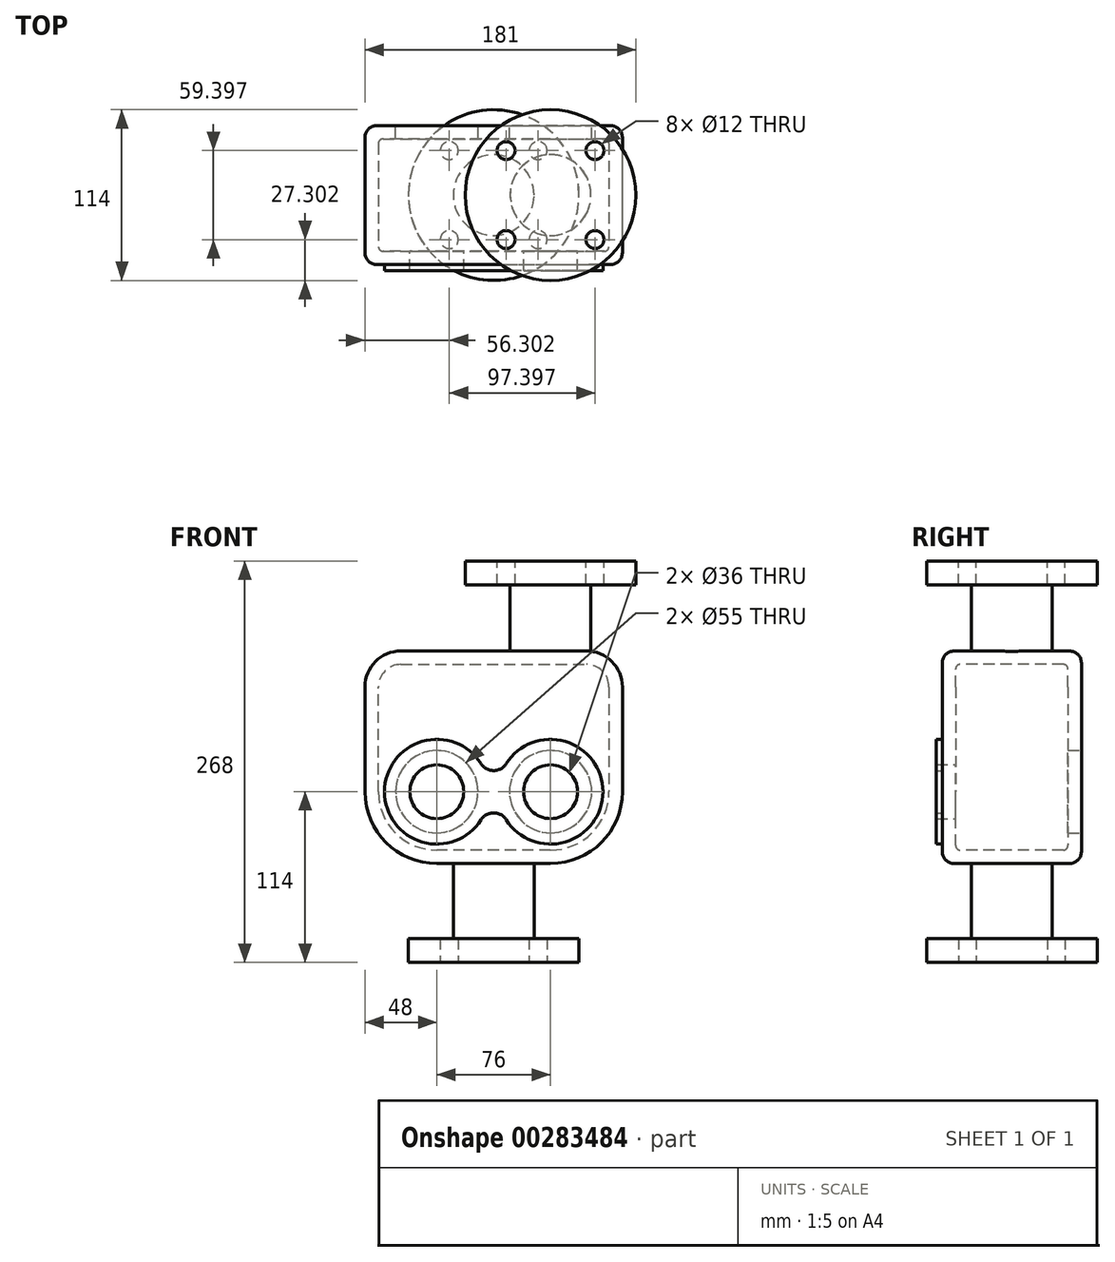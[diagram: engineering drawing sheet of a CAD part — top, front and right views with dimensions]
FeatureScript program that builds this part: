
annotation { "Feature Type Name" : "Feature", "Feature Type Description" : "" }
export const myFeature = defineFeature(function(context is Context, id is Id, definition is map)
    precondition{}
    {
        {
            var Q0;
            Q0=qCreatedBy(makeId("Top.planeOp"),FACE);
            var sketch = newSketch(context, id + "F0", { "sketchPlane" : qUnion([Q0])});
            skCircle(sketch, "E0", {"center": v(0, 0) * mm, "radius": 57 * mm});
            skCircle(sketch, "E1", {"center": v(0, 0) * mm, "radius": 42 * mm, "construction": true});
            skCircle(sketch, "E2", {"center": v(29.7, -29.7) * mm, "radius": 6 * mm});
            skLineSegment(sketch, "E3", {"start": v(0, 0) * mm, "end": v(29.7, -29.7) * mm, "construction": true});
            skCircle(sketch, "E4.MirrorC", {"center": v(-29.7, -29.7) * mm, "radius": 6 * mm});
            skCircle(sketch, "E5.MirrorC", {"center": v(-29.7, 29.7) * mm, "radius": 6 * mm});
            skCircle(sketch, "E6.MirrorC", {"center": v(29.7, 29.7) * mm, "radius": 6 * mm});
            skSolve(sketch);
        }
        {
            var Q0;
            Q0=makeQuery(id+"F0.imprint","IMPRINT",FACE,{"disambiguationData":[TD([[makeQuery(id+"F0.imprint","IMPRINT",EDGE,{"derivedFrom":sQuery(id+"F0.wireOp",EDGE,"E0")}),1.0]])]});
            extrude(context, id + "F1", {"entities" : qUnion([Q0]), "depth" : 16 * mm});
        }
        {
            var Q0;
            Q0=makeQuery(id+"F1.opExtrude","CAP_FACE",FACE,{"disambiguationData":[OSD([sQuery(id+"F0.wireOp",EDGE,"E0"),sQuery(id+"F0.wireOp",EDGE,"E2"),sQuery(id+"F0.wireOp",EDGE,"E4.MirrorC"),sQuery(id+"F0.wireOp",EDGE,"E5.MirrorC"),sQuery(id+"F0.wireOp",EDGE,"E6.MirrorC")])],"isStart":false});
            var sketch = newSketch(context, id + "F2", { "sketchPlane" : qUnion([Q0])});
            skCircle(sketch, "E7", {"center": v(0, 0) * mm, "radius": 27 * mm});
            skSolve(sketch);
        }
        {
            var Q0;
            Q0=makeQuery(id+"F2.imprint","IMPRINT",FACE,{"disambiguationData":[TD([[makeQuery(id+"F2.imprint","IMPRINT",EDGE,{"derivedFrom":sQuery(id+"F2.wireOp",EDGE,"E7")}),1.0]])]});
            extrude(context, id + "F3", {"entities" : qUnion([Q0]), "operationType" : NewBodyOperationType.ADD, "depth" : 50 * mm});
        }
        {
            var Q0;
            Q0=qCreatedBy(makeId("Front.planeOp"),FACE);
            var sketch = newSketch(context, id + "F4", { "sketchPlane" : qUnion([Q0])});
            skLineSegment(sketch, "E8.bottom", {"start": v(-62, 208) * mm, "end": v(62, 208) * mm});
            skLineSegment(sketch, "E8.top", {"start": v(-86, 114) * mm, "end": v(86, 114) * mm, "construction": true});
            skLineSegment(sketch, "E8.left", {"start": v(-86, 184) * mm, "end": v(-86, 114) * mm});
            skLineSegment(sketch, "E8.right", {"start": v(86, 184) * mm, "end": v(86, 114) * mm});
            skLineSegment(sketch, "E9", {"start": v(0, 0) * mm, "end": v(0, 370.93) * mm, "construction": true});
            skArc(sketch, "E10", {"start": v(-86, 114) * mm, "mid": v(-71.94, 80.06) * mm, "end": v(-38, 66) * mm});
            skLineSegment(sketch, "E11", {"start": v(-38, 66) * mm, "end": v(0, 66) * mm});
            skArc(sketch, "E12.MirrorCS", {"start": v(86, 114) * mm, "mid": v(71.94, 80.06) * mm, "end": v(38, 66) * mm});
            skLineSegment(sketch, "E13", {"start": v(0, 66) * mm, "end": v(38, 66) * mm});
            skPoint(sketch, "E14.visualSharp", {"position": v(86, 208) * mm});
            skArc(sketch, "E14.filletArc", {"start": v(86, 184) * mm, "mid": v(78.97, 200.97) * mm, "end": v(62, 208) * mm});
            skPoint(sketch, "E15.visualSharp", {"position": v(-86, 208) * mm});
            skArc(sketch, "E15.filletArc", {"start": v(-62, 208) * mm, "mid": v(-78.97, 200.97) * mm, "end": v(-86, 184) * mm});
            skSolve(sketch);
        }
        {
            var Q0;
            Q0=makeQuery(id+"F4.imprint","IMPRINT",FACE,{"disambiguationData":[TD([[makeQuery(id+"F4.imprint","IMPRINT",EDGE,{"derivedFrom":sQuery(id+"F4.wireOp",EDGE,"E8.bottom")}),-1.0]])]});
            extrude(context, id + "F5", {"entities" : qUnion([Q0]), "operationType" : NewBodyOperationType.ADD, "endBound" : BoundingType.SYMMETRIC, "depth" : 93 * mm});
        }
        {
            var Q0;
            Q0=makeQuery(id+"F5.opExtrude","CAP_FACE",FACE,{"disambiguationData":[OSD([sQuery(id+"F4.wireOp",EDGE,"E8.bottom"),sQuery(id+"F4.wireOp",EDGE,"E8.left"),sQuery(id+"F4.wireOp",EDGE,"E8.right"),sQuery(id+"F4.wireOp",EDGE,"E10"),sQuery(id+"F4.wireOp",EDGE,"E11"),sQuery(id+"F4.wireOp",EDGE,"E12.MirrorCS"),sQuery(id+"F4.wireOp",EDGE,"E13"),sQuery(id+"F4.wireOp",EDGE,"E14.filletArc"),sQuery(id+"F4.wireOp",EDGE,"E15.filletArc")])],"isStart":false});
            var Q1;
            Q1=makeQuery(id+"F5.opExtrude","CAP_FACE",FACE,{"disambiguationData":[OSD([sQuery(id+"F4.wireOp",EDGE,"E8.bottom"),sQuery(id+"F4.wireOp",EDGE,"E8.left"),sQuery(id+"F4.wireOp",EDGE,"E8.right"),sQuery(id+"F4.wireOp",EDGE,"E10"),sQuery(id+"F4.wireOp",EDGE,"E11"),sQuery(id+"F4.wireOp",EDGE,"E12.MirrorCS"),sQuery(id+"F4.wireOp",EDGE,"E13"),sQuery(id+"F4.wireOp",EDGE,"E14.filletArc"),sQuery(id+"F4.wireOp",EDGE,"E15.filletArc")])],"isStart":true});
            fillet(context, id + "F6", {"entities" : qUnion([Q0, Q1]), "radius" : 8 * mm, "tangentPropagation" : true, "allowEdgeOverflow" : false});
        }
        {
            var Q0;
            Q0=makeQuery(id+"F5.opExtrude","SWEPT_FACE",FACE,{"disambiguationData":[OSD([sQuery(id+"F4.wireOp",EDGE,"E8.bottom")])]});
            var sketch = newSketch(context, id + "F7", { "sketchPlane" : qUnion([Q0])});
            skCircle(sketch, "E16", {"center": v(38, 0) * mm, "radius": 27 * mm});
            skSolve(sketch);
        }
        {
            var Q0;
            Q0 = qSketchRegion(id + "F7", true);
            extrude(context, id + "F8", {"entities" : qUnion([Q0]), "operationType" : NewBodyOperationType.ADD, "depth" : 44 * mm, "hasSecondDirection" : true, "secondDirectionOppositeDirection" : true, "secondDirectionDepth" : 25 * mm});
        }
        {
            var Q0;
            Q0=makeQuery(id+"F8.opExtrude","CAP_FACE",FACE,{"disambiguationData":[OSD([sQuery(id+"F7.wireOp",EDGE,"E16")])],"isStart":false});
            var sketch = newSketch(context, id + "F9", { "sketchPlane" : qUnion([Q0])});
            skCircle(sketch, "E17", {"center": v(38, 0) * mm, "radius": 57 * mm});
            skSolve(sketch);
        }
        {
            var Q0;
            Q0=makeQuery(id+"F9.imprint","IMPRINT",FACE,{"disambiguationData":[TD([[makeQuery(id+"F9.imprint","IMPRINT",EDGE,{"derivedFrom":sQuery(id+"F9.wireOp",EDGE,"E17")}),1.0]])]});
            var Q1;
            Q1=makeQuery(id+"F9.imprint","IMPRINT",FACE,{"disambiguationData":[TD([[makeQuery(id+"F9.imprint","IMPRINT",EDGE,{"derivedFrom":makeQuery(id+"F8.opExtrude","CAP_EDGE",EDGE,{"disambiguationData":[OSD([sQuery(id+"F7.wireOp",EDGE,"E16")])],"isStart":false})}),1.0]])]});
            extrude(context, id + "F10", {"entities" : qUnion([Q0, Q1]), "operationType" : NewBodyOperationType.ADD, "depth" : 16 * mm});
        }
        {
            var Q0;
            Q0=makeQuery(id+"F10.opExtrude","CAP_FACE",FACE,{"disambiguationData":[OSD([sQuery(id+"F9.wireOp",EDGE,"E17")])],"isStart":false});
            var sketch = newSketch(context, id + "F11", { "sketchPlane" : qUnion([Q0])});
            skCircle(sketch, "E18", {"center": v(38, 0) * mm, "radius": 15.68 * mm, "construction": true});
            skLineSegment(sketch, "E19", {"start": v(38, 0) * mm, "end": v(94.43, 56.43) * mm, "construction": true});
            skLineSegment(sketch, "E20", {"start": v(38, 0) * mm, "end": v(117.44, 0) * mm, "construction": true});
            skCircle(sketch, "E21", {"center": v(67.7, 29.7) * mm, "radius": 6 * mm});
            skLineSegment(sketch, "E22", {"start": v(38, 0) * mm, "end": v(38, 52.6) * mm, "construction": true});
            skCircle(sketch, "E23.MirrorC", {"center": v(67.7, -29.7) * mm, "radius": 6 * mm});
            skCircle(sketch, "E24.MirrorC", {"center": v(8.3, 29.7) * mm, "radius": 6 * mm});
            skCircle(sketch, "E25.MirrorC", {"center": v(8.3, -29.7) * mm, "radius": 6 * mm});
            skSolve(sketch);
        }
        {
            var Q0;
            Q0 = qSketchRegion(id + "F11", true);
            extrude(context, id + "F12", {"entities" : qUnion([Q0]), "operationType" : NewBodyOperationType.REMOVE, "oppositeDirection" : true, "depth" : 25 * mm});
        }
        {
            var Q0;
            Q0=qCreatedBy(makeId("Front.planeOp"),FACE);
            var sketch = newSketch(context, id + "F13", { "sketchPlane" : qUnion([Q0])});
            skArc(sketch, "E26.0", {"start": v(-38, 75) * mm, "mid": v(-65.58, 86.42) * mm, "end": v(-77, 114) * mm});
            skLineSegment(sketch, "E26.1", {"start": v(38, 75) * mm, "end": v(-38, 75) * mm});
            skLineSegment(sketch, "E26.2", {"start": v(-77, 114) * mm, "end": v(-77, 184) * mm});
            skArc(sketch, "E26.3", {"start": v(77, 114) * mm, "mid": v(65.58, 86.42) * mm, "end": v(38, 75) * mm});
            skArc(sketch, "E26.4", {"start": v(-77, 184) * mm, "mid": v(-72.6, 194.6) * mm, "end": v(-62, 199) * mm});
            skLineSegment(sketch, "E26.5", {"start": v(-62, 199) * mm, "end": v(62, 199) * mm});
            skArc(sketch, "E26.6", {"start": v(62, 199) * mm, "mid": v(72.6, 194.6) * mm, "end": v(77, 184) * mm});
            skLineSegment(sketch, "E26.7", {"start": v(77, 184) * mm, "end": v(77, 114) * mm});
            skSolve(sketch);
        }
        {
            var Q0;
            Q0 = qSketchRegion(id + "F13", true);
            extrude(context, id + "F14", {"entities" : qUnion([Q0]), "operationType" : NewBodyOperationType.REMOVE, "endBound" : BoundingType.SYMMETRIC, "oppositeDirection" : true, "depth" : 75 * mm});
        }
        {
            var Q0;
            Q0=makeQuery(id+"F14.boolean.opBoolean","COPY",EDGE,{"derivedFrom":makeQuery(id+"F14.opExtrude","CAP_EDGE",EDGE,{"disambiguationData":[OSD([sQuery(id+"F13.wireOp",EDGE,"E26.7")])],"isStart":false})});
            fillet(context, id + "F15", {"entities" : qUnion([Q0]), "radius" : 3 * mm, "tangentPropagation" : true, "allowEdgeOverflow" : false});
        }
        {
            var Q0;
            Q0=makeQuery(id+"F14.boolean.opBoolean","COPY",EDGE,{"derivedFrom":makeQuery(id+"F14.opExtrude","CAP_EDGE",EDGE,{"disambiguationData":[OSD([sQuery(id+"F13.wireOp",EDGE,"E26.7")])],"isStart":true})});
            fillet(context, id + "F16", {"entities" : qUnion([Q0]), "radius" : 3 * mm, "tangentPropagation" : true, "allowEdgeOverflow" : false});
        }
        {
            var Q0;
            Q0=makeQuery(id+"F5.opExtrude","CAP_FACE",FACE,{"disambiguationData":[OSD([sQuery(id+"F4.wireOp",EDGE,"E8.bottom"),sQuery(id+"F4.wireOp",EDGE,"E8.left"),sQuery(id+"F4.wireOp",EDGE,"E8.right"),sQuery(id+"F4.wireOp",EDGE,"E10"),sQuery(id+"F4.wireOp",EDGE,"E11"),sQuery(id+"F4.wireOp",EDGE,"E12.MirrorCS"),sQuery(id+"F4.wireOp",EDGE,"E13"),sQuery(id+"F4.wireOp",EDGE,"E14.filletArc"),sQuery(id+"F4.wireOp",EDGE,"E15.filletArc")])],"isStart":false});
            var sketch = newSketch(context, id + "F17", { "sketchPlane" : qUnion([Q0])});
            skCircle(sketch, "E27", {"center": v(38, 114) * mm, "radius": 35 * mm});
            skCircle(sketch, "E28", {"center": v(-38, 114) * mm, "radius": 35 * mm});
            skCircle(sketch, "E29", {"center": v(-38, 114) * mm, "radius": 18 * mm});
            skCircle(sketch, "E30", {"center": v(38, 114) * mm, "radius": 18 * mm});
            skArc(sketch, "E31", {"start": v(-8.44, 132.75) * mm, "mid": v(0, 128.1) * mm, "end": v(8.44, 132.75) * mm});
            skArc(sketch, "E32", {"start": v(8.44, 95.25) * mm, "mid": v(0, 99.9) * mm, "end": v(-8.44, 95.25) * mm});
            skSolve(sketch);
        }
        {
            var Q0;
            Q0 = qSketchRegion(id + "F17", true);
            extrude(context, id + "F18", {"entities" : qUnion([Q0]), "operationType" : NewBodyOperationType.ADD, "depth" : 4 * mm});
        }
        {
            var Q0;
            Q0=makeQuery(id+"F18.boolean.opBoolean","SPLIT",FACE,{"disambiguationData":[TD([makeQuery(id+"F18.opExtrude","SWEPT_FACE",FACE,{"disambiguationData":[OSD([sQuery(id+"F17.wireOp",EDGE,"E29")])]})])],"derivedFrom":makeQuery(id+"F5.opExtrude","CAP_FACE",FACE,{"disambiguationData":[OSD([sQuery(id+"F4.wireOp",EDGE,"E8.bottom"),sQuery(id+"F4.wireOp",EDGE,"E8.left"),sQuery(id+"F4.wireOp",EDGE,"E8.right"),sQuery(id+"F4.wireOp",EDGE,"E10"),sQuery(id+"F4.wireOp",EDGE,"E11"),sQuery(id+"F4.wireOp",EDGE,"E12.MirrorCS"),sQuery(id+"F4.wireOp",EDGE,"E13"),sQuery(id+"F4.wireOp",EDGE,"E14.filletArc"),sQuery(id+"F4.wireOp",EDGE,"E15.filletArc")])],"isStart":false})});
            var Q1;
            Q1=makeQuery(id+"F18.boolean.opBoolean","SPLIT",FACE,{"disambiguationData":[TD([makeQuery(id+"F18.opExtrude","SWEPT_FACE",FACE,{"disambiguationData":[OSD([sQuery(id+"F17.wireOp",EDGE,"E30")])]})])],"derivedFrom":makeQuery(id+"F5.opExtrude","CAP_FACE",FACE,{"disambiguationData":[OSD([sQuery(id+"F4.wireOp",EDGE,"E8.bottom"),sQuery(id+"F4.wireOp",EDGE,"E8.left"),sQuery(id+"F4.wireOp",EDGE,"E8.right"),sQuery(id+"F4.wireOp",EDGE,"E10"),sQuery(id+"F4.wireOp",EDGE,"E11"),sQuery(id+"F4.wireOp",EDGE,"E12.MirrorCS"),sQuery(id+"F4.wireOp",EDGE,"E13"),sQuery(id+"F4.wireOp",EDGE,"E14.filletArc"),sQuery(id+"F4.wireOp",EDGE,"E15.filletArc")])],"isStart":false})});
            extrude(context, id + "F19", {"entities" : qUnion([Q0, Q1]), "operationType" : NewBodyOperationType.REMOVE, "oppositeDirection" : true, "depth" : 25 * mm});
        }
        {
            var Q0;
            Q0=makeQuery(id+"F5.opExtrude","CAP_FACE",FACE,{"disambiguationData":[OSD([sQuery(id+"F4.wireOp",EDGE,"E8.bottom"),sQuery(id+"F4.wireOp",EDGE,"E8.left"),sQuery(id+"F4.wireOp",EDGE,"E8.right"),sQuery(id+"F4.wireOp",EDGE,"E10"),sQuery(id+"F4.wireOp",EDGE,"E11"),sQuery(id+"F4.wireOp",EDGE,"E12.MirrorCS"),sQuery(id+"F4.wireOp",EDGE,"E13"),sQuery(id+"F4.wireOp",EDGE,"E14.filletArc"),sQuery(id+"F4.wireOp",EDGE,"E15.filletArc")])],"isStart":true});
            var sketch = newSketch(context, id + "F20", { "sketchPlane" : qUnion([Q0])});
            skCircle(sketch, "E33.0", {"center": v(-38, 114) * mm, "radius": 18 * mm, "construction": true});
            skCircle(sketch, "E34.0", {"center": v(38, 114) * mm, "radius": 18 * mm, "construction": true});
            skCircle(sketch, "E35", {"center": v(-38, 114) * mm, "radius": 27.5 * mm});
            skCircle(sketch, "E36", {"center": v(38, 114) * mm, "radius": 27.5 * mm});
            skSolve(sketch);
        }
        {
            var Q0;
            Q0 = qSketchRegion(id + "F20", true);
            extrude(context, id + "F21", {"entities" : qUnion([Q0]), "operationType" : NewBodyOperationType.REMOVE, "oppositeDirection" : true, "depth" : 25 * mm});
        }
    });
